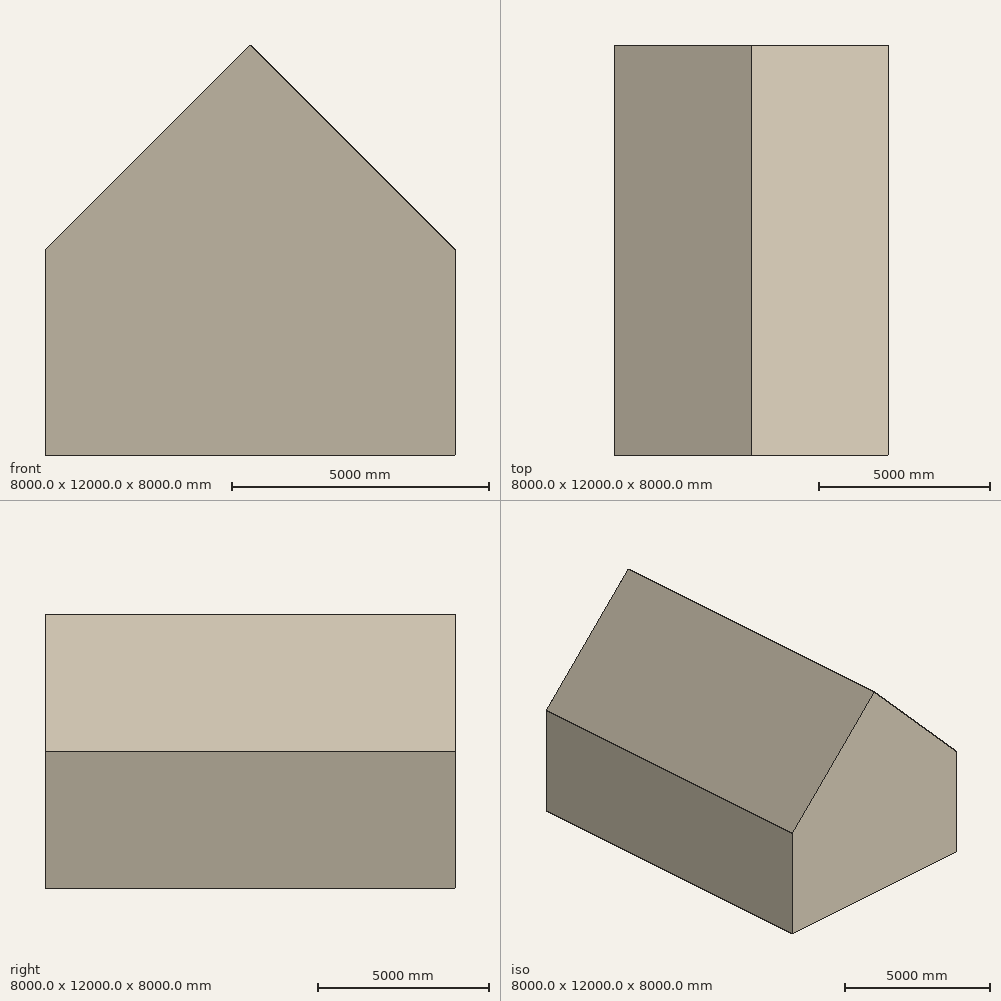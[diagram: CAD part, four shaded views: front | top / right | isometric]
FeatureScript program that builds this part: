
annotation { "Feature Type Name" : "Feature", "Feature Type Description" : "" }
export const myFeature = defineFeature(function(context is Context, id is Id, definition is map)
    precondition{}
    {
        {
            var Q0;
            Q0=qCreatedBy(makeId("Front.planeOp"),FACE);
            var sketch = newSketch(context, id + "F0", { "sketchPlane" : qUnion([Q0])});
            skLineSegment(sketch, "E0.bottom", {"start": v(-4000, 1247.99) * mm, "end": v(4000, 1247.99) * mm});
            skLineSegment(sketch, "E0.top", {"start": v(-4000, -2752.01) * mm, "end": v(4000, -2752.01) * mm});
            skLineSegment(sketch, "E0.left", {"start": v(-4000, 1247.99) * mm, "end": v(-4000, -2752.01) * mm});
            skLineSegment(sketch, "E0.right", {"start": v(4000, 1247.99) * mm, "end": v(4000, -2752.01) * mm});
            skLineSegment(sketch, "E1", {"start": v(0, 1247.99) * mm, "end": v(0, 5247.99) * mm});
            skLineSegment(sketch, "E2", {"start": v(-4000, 1247.99) * mm, "end": v(0, 5247.99) * mm});
            skLineSegment(sketch, "E3", {"start": v(0, 5247.99) * mm, "end": v(4000, 1247.99) * mm});
            skSolve(sketch);
        }
        {
            var Q0;
            Q0 = qSketchRegion(id + "F0", true);
            extrude(context, id + "F1", {"entities" : qUnion([Q0]), "depth" : 12000 * mm});
        }
    });
